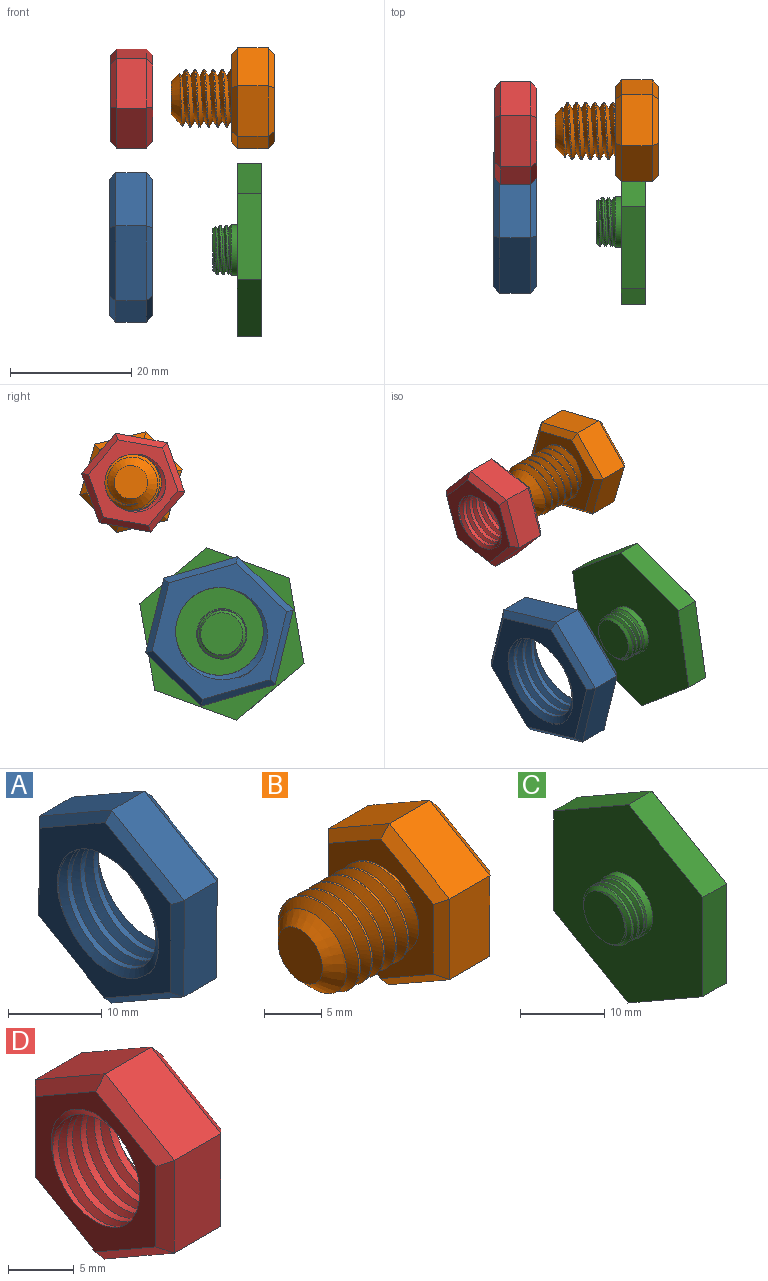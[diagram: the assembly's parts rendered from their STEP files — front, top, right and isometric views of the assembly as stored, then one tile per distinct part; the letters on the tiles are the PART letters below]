
ASSEMBLY  parts=4 mates=2
PART A: 23 faces, bbox 9.3x22.7x26 mm
  f0: cylinder r=7.24mm len=14.48mm, axis (1,0,0), area 111.6mm2, adj f7,f8,f21,f22
  f1: plane 10.98x6.38mm, normal (0,-0.5,0.86), area 63.5mm2, adj f2,f6,f14,f18
  f2: plane 12.7x5mm, normal (0,-1,0), area 63.5mm2, adj f1,f3,f12,f16
  f3: plane 11.02x6.32mm, normal (0,-0.5,-0.87), area 63.5mm2, adj f2,f4,f10,f15
  f4: plane 10.98x6.38mm, normal (0,0.5,-0.86), area 63.5mm2, adj f3,f5,f9,f17
  f5: plane 12.7x5mm, normal (0,1,0), area 63.5mm2, adj f4,f6,f11,f19
  f6: plane 11.02x6.32mm, normal (0,0.5,0.87), area 63.5mm2, adj f1,f5,f13,f20
  f7: plane 23.73x20.67mm, normal (-1,0,0), area 164.4mm2, adj f0,f9,f10,f11,f12,f13,f14,f21
  f8: plane 23.73x20.67mm, normal (1,0,0), area 164.4mm2, adj f0,f15,f16,f17,f18,f19,f20,f21
  f9: plane 10.99x6.96mm, normal (-0.71,0.36,-0.61), area 17.1mm2, adj f4,f7,f10,f11
  f10: plane 11.02x6.9mm, normal (-0.71,-0.35,-0.61), area 17.1mm2, adj f3,f7,f9,f12
  f11: plane 12.7x1.03mm, normal (-0.71,0.71,0), area 17.1mm2, adj f5,f7,f9,f13
  f12: plane 12.7x1.03mm, normal (-0.71,-0.71,0), area 17.1mm2, adj f2,f7,f10,f14
  f13: plane 11.02x6.9mm, normal (-0.71,0.35,0.61), area 17.1mm2, adj f6,f7,f11,f14
  f14: plane 10.99x6.96mm, normal (-0.71,-0.36,0.61), area 17.1mm2, adj f1,f7,f12,f13
  f15: plane 11.02x6.9mm, normal (0.71,-0.35,-0.61), area 17.1mm2, adj f3,f8,f16,f17
  f16: plane 12.7x1.03mm, normal (0.71,-0.71,0), area 17.1mm2, adj f2,f8,f15,f18
  f17: plane 10.99x6.96mm, normal (0.71,0.36,-0.61), area 17.1mm2, adj f4,f8,f15,f19
  f18: plane 10.99x6.96mm, normal (0.71,-0.36,0.61), area 17.1mm2, adj f1,f8,f16,f20
  f19: plane 12.7x1.03mm, normal (0.71,0.71,0), area 17.1mm2, adj f5,f8,f17,f20
  f20: plane 11.02x6.9mm, normal (0.71,0.35,0.61), area 17.1mm2, adj f6,f8,f18,f19
  f21: bspline ~19.31x16.73mm, area 223mm2, adj f0,f7,f8,f22
  f22: bspline ~19.31x16.73mm, area 223mm2, adj f0,f7,f8,f21
PART B: 25 faces, bbox 17.8x15.9x18.1 mm
  f0: cylinder r=4.75mm len=9.5mm, axis (1,0,0), area 28.1mm2, adj f1,f2,f4,f12
  f1: bspline ~10.97x9.91mm, area 196.7mm2, adj f0,f2,f4,f12
  f2: bspline ~10.97x10.66mm, area 196.6mm2, adj f0,f1,f4,f12
  f3: plane 5.5x5.5mm, normal (-1,0,0), area 23.8mm2, adj f4
  f4: cone r=4.75mm half-angle=45deg, axis (1,0,0), area 47.4mm2, adj f0,f1,f2,f3
  f5: plane 7.48x5mm, normal (0,-0.5,0.86), area 43.3mm2, adj f6,f10,f18,f22
  f6: plane 8.66x5mm, normal (0,-1,0), area 43.3mm2, adj f5,f7,f16,f20
  f7: plane 7.52x5mm, normal (0,-0.5,-0.87), area 43.3mm2, adj f6,f8,f14,f19
  f8: plane 7.48x5mm, normal (0,0.5,-0.86), area 43.3mm2, adj f7,f9,f13,f21
  f9: plane 8.66x5mm, normal (0,1,0), area 43.3mm2, adj f8,f10,f15,f23
  f10: plane 7.52x5mm, normal (0,0.5,0.87), area 43.3mm2, adj f5,f9,f17,f24
  f11: plane 15.01x13.03mm, normal (1,0,0), area 146.4mm2, adj f13,f14,f15,f16,f17,f18
  f12: plane 15.83x13.85mm, normal (-1,0,0), area 89.2mm2, adj f0,f1,f2,f19,f20,f21,f22,f23
  f13: plane 7.49x4.93mm, normal (0.71,0.36,-0.61), area 11.4mm2, adj f8,f11,f14,f15
  f14: plane 7.52x4.88mm, normal (0.71,-0.35,-0.61), area 11.4mm2, adj f7,f11,f13,f16
  f15: plane 8.66x1.03mm, normal (0.71,0.71,0), area 11.4mm2, adj f9,f11,f13,f17
  f16: plane 8.66x1.03mm, normal (0.71,-0.71,0), area 11.4mm2, adj f6,f11,f14,f18
  f17: plane 7.52x4.88mm, normal (0.71,0.35,0.61), area 11.4mm2, adj f10,f11,f15,f18
  f18: plane 7.49x4.93mm, normal (0.71,-0.36,0.61), area 11.4mm2, adj f5,f11,f16,f17
  f19: plane 7.52x4.88mm, normal (-0.71,-0.35,-0.61), area 11.4mm2, adj f7,f12,f20,f21
  f20: plane 8.66x1.03mm, normal (-0.71,-0.71,0), area 11.4mm2, adj f6,f12,f19,f22
  f21: plane 7.49x4.93mm, normal (-0.71,0.36,-0.61), area 11.4mm2, adj f8,f12,f19,f23
  f22: plane 7.49x4.93mm, normal (-0.71,-0.36,0.61), area 11.4mm2, adj f5,f12,f20,f24
  f23: plane 8.66x1.03mm, normal (-0.71,0.71,0), area 11.4mm2, adj f9,f12,f21,f24
  f24: plane 7.52x4.88mm, normal (-0.71,0.35,0.61), area 11.4mm2, adj f10,f12,f22,f23
PART C: 22 faces, bbox 8.5x25.1x28.9 mm
  f0: plane 12.48x7.25mm, normal (0,-0.5,0.86), area 57.3mm2, adj f1,f5,f7,f13
  f1: plane 14.43x3.97mm, normal (0,-1,0), area 57.3mm2, adj f0,f2,f7,f11
  f2: plane 12.52x7.18mm, normal (0,-0.5,-0.87), area 57.3mm2, adj f1,f3,f7,f9
  f3: plane 12.48x7.25mm, normal (0,0.5,-0.86), area 57.3mm2, adj f2,f4,f7,f8
  f4: plane 14.43x3.97mm, normal (0,1,0), area 57.3mm2, adj f3,f5,f7,f10
  f5: plane 12.52x7.18mm, normal (0,0.5,0.87), area 57.3mm2, adj f0,f4,f7,f12
  f6: plane 28.8x24.98mm, normal (1,0,0), area 538.7mm2, adj f8,f9,f10,f11,f12,f13
  f7: plane 28.87x25.04mm, normal (-1,0,0), area 487.2mm2, adj f0,f1,f2,f3,f4,f5,f14
  f8: plane 12.48x7.27mm, normal (0.71,0.36,-0.61), area 0.6mm2, adj f3,f6,f9,f10
  f9: plane 12.52x7.2mm, normal (0.71,-0.35,-0.61), area 0.6mm2, adj f2,f6,f8,f11
  f10: plane 14.43x0.07mm, normal (0.71,0.71,0), area 0.6mm2, adj f4,f6,f8,f12
  f11: plane 14.43x0.07mm, normal (0.71,-0.71,0), area 0.6mm2, adj f1,f6,f9,f13
  f12: plane 12.52x7.2mm, normal (0.71,0.35,0.61), area 0.6mm2, adj f5,f6,f10,f13
  f13: plane 12.48x7.27mm, normal (0.71,-0.36,0.61), area 0.6mm2, adj f0,f6,f11,f12
  f14: cylinder r=4.15mm len=8.3mm, axis (1,0,0), area 26.1mm2, adj f7,f20
  f15: cone r=3.98mm half-angle=45deg, axis (1,0,0), area 10.2mm2, adj f16,f17,f18,f19
  f16: plane 6.99x6.92mm, normal (-1,0,0), area 38.1mm2, adj f15,f17,f18
  f17: bspline ~9.2x7.97mm, area 36.1mm2, adj f15,f16,f18,f19,f20,f21
  f18: bspline ~9.2x7.97mm, area 36.1mm2, adj f15,f16,f17,f19,f20,f21
  f19: cylinder r=3.98mm len=7.97mm, axis (1,0,0), area 19.6mm2, adj f15,f17,f18,f20
  f20: cone r=3.15mm half-angle=45deg, axis (1,0,0), area 10.8mm2, adj f14,f17,f18,f19,f21
  f21: cone r=3.15mm half-angle=45deg, axis (1,0,0), area 1.7mm2, adj f17,f18,f20
PART D: 23 faces, bbox 9.1x15.4x17.7 mm
  f0: plane 7.49x5mm, normal (0,-0.5,0.86), area 43.3mm2, adj f1,f5,f13,f17
  f1: plane 8.66x5mm, normal (0,-1,0), area 43.3mm2, adj f0,f2,f11,f15
  f2: plane 7.51x5mm, normal (0,-0.5,-0.87), area 43.3mm2, adj f1,f3,f9,f14
  f3: plane 7.49x5mm, normal (0,0.5,-0.86), area 43.3mm2, adj f2,f4,f8,f16
  f4: plane 8.66x5mm, normal (0,1,0), area 43.3mm2, adj f3,f5,f10,f18
  f5: plane 7.51x5mm, normal (0,0.5,0.87), area 43.3mm2, adj f0,f4,f12,f19
  f6: plane 15.37x13.38mm, normal (-1,0,0), area 71.4mm2, adj f8,f9,f10,f11,f12,f13,f20,f21
  f7: plane 15.37x13.38mm, normal (1,0,0), area 71.4mm2, adj f14,f15,f16,f17,f18,f19,f20,f21
  f8: plane 7.49x4.93mm, normal (-0.71,0.36,-0.61), area 11.4mm2, adj f3,f6,f9,f10
  f9: plane 7.51x4.89mm, normal (-0.71,-0.35,-0.61), area 11.4mm2, adj f2,f6,f8,f11
  f10: plane 8.66x1.02mm, normal (-0.71,0.71,0), area 11.4mm2, adj f4,f6,f8,f12
  f11: plane 8.66x1.02mm, normal (-0.71,-0.71,0), area 11.4mm2, adj f1,f6,f9,f13
  f12: plane 7.51x4.89mm, normal (-0.71,0.35,0.61), area 11.4mm2, adj f5,f6,f10,f13
  f13: plane 7.49x4.93mm, normal (-0.71,-0.36,0.61), area 11.4mm2, adj f0,f6,f11,f12
  f14: plane 7.51x4.89mm, normal (0.71,-0.35,-0.61), area 11.4mm2, adj f2,f7,f15,f16
  f15: plane 8.66x1.02mm, normal (0.71,-0.71,0), area 11.4mm2, adj f1,f7,f14,f17
  f16: plane 7.49x4.93mm, normal (0.71,0.36,-0.61), area 11.4mm2, adj f3,f7,f14,f18
  f17: plane 7.49x4.93mm, normal (0.71,-0.36,0.61), area 11.4mm2, adj f0,f7,f15,f19
  f18: plane 8.66x1.02mm, normal (0.71,0.71,0), area 11.4mm2, adj f4,f7,f16,f19
  f19: plane 7.51x4.89mm, normal (0.71,0.35,0.61), area 11.4mm2, adj f5,f7,f17,f18
  f20: cylinder r=4.66mm len=9.32mm, axis (1,0,0), area 85.4mm2, adj f6,f7,f21,f22
  f21: bspline ~12.5x10.82mm, area 128.4mm2, adj f6,f7,f20,f22
  f22: bspline ~12.5x10.82mm, area 128.5mm2, adj f6,f7,f20,f21
PLACE A rot(axis=(0,0.6,-0.8),180deg) t=(-55.27,-6.86,23.48)mm fixed
PLACE B rot(axis=(-1,0,0),43.8deg) t=(-31.66,7.73,48.08)mm
PLACE C rot(axis=(1,0,0),109.9deg) t=(-32.27,-7.25,23.06)mm
PLACE D rot(axis=(1,0,0),100.2deg) t=(-48.16,7.38,48.02)mm fixed
MATE cylindrical C.f15 <-> A.f7  axis (-1,0,0) through (-38.27,-7.25,23.06)mm
MATE cylindrical B.f0 <-> D.f6  axis (-1,0,0) through (-45.16,7.73,48.08)mm
